# Revit family: Haworth_Epure_UserFriendlyExtensionDesk_EU_PRELIMINARY
name_source: partatom
category: Furniture
units: mm (PartAtom-declared; Revit-internal decimal feet)

## family parameters
Always vertical = Yes
Cut with Voids When Loaded = No
OmniClass Number = 23.40.70.14.64.11
OmniClass Title = Office Furniture
Room Calculation Point = No
Shared = No
Work Plane-Based = No

## types (8) — shared parameters
120 x 40 - rounded = No
140 x 30 - squared = No
160 x 30 - rounded = No
160 x 50 - squared = No
180 x 30 - rounded = No
3/4 130 - squared = No
80 x 30 - rounded = No
80 x 80 - squared = No
Actual Depth = 100 cm
Actual Height = 73 cm
Actual Width = 180 cm
Assembly Code = E2020200
Description = Haworth - Epure - User-Friendly Extension Desk
Leg Height = 70 cm
Manufacturer = Haworth
Model = EUUFXXXX
Revision Number = 1
Size = Verify Final Dim.w/ Haworth
Trim Finish = Haworth _ Metal _ Structured White EC
URL = https://www.haworth.com
URL - Product = https://www.haworth.com
Warranty = http://www.haworth.com

## per-type parameters (varying)
| type | Angled Leg | One Leg | Rounded Corners | Squared Corners | Two Legs |
| 120 x 40 - squared | No | Yes | No | Yes | No |
| 140 x 30 - rounded | No | Yes | Yes | No | No |
| 160 x 30 - squared | No | Yes | No | Yes | No |
| 160 x 50 - rounded | No | Yes | Yes | No | No |
| 180 x 30 - squared | No | Yes | No | Yes | No |
| 3/4 130 - rounded | Yes | No | Yes | No | No |
| 80 x 30 - squared | No | Yes | No | Yes | No |
| 80 x 80 - rounded | No | No | Yes | No | Yes |

type visibility flags: 8 boolean params named "<type name>" — each type sets only its own to Yes (folded from table)

## geometry (parser evidence)
native form markers: Sweep x7
no freeform markers — native parametric forms only
